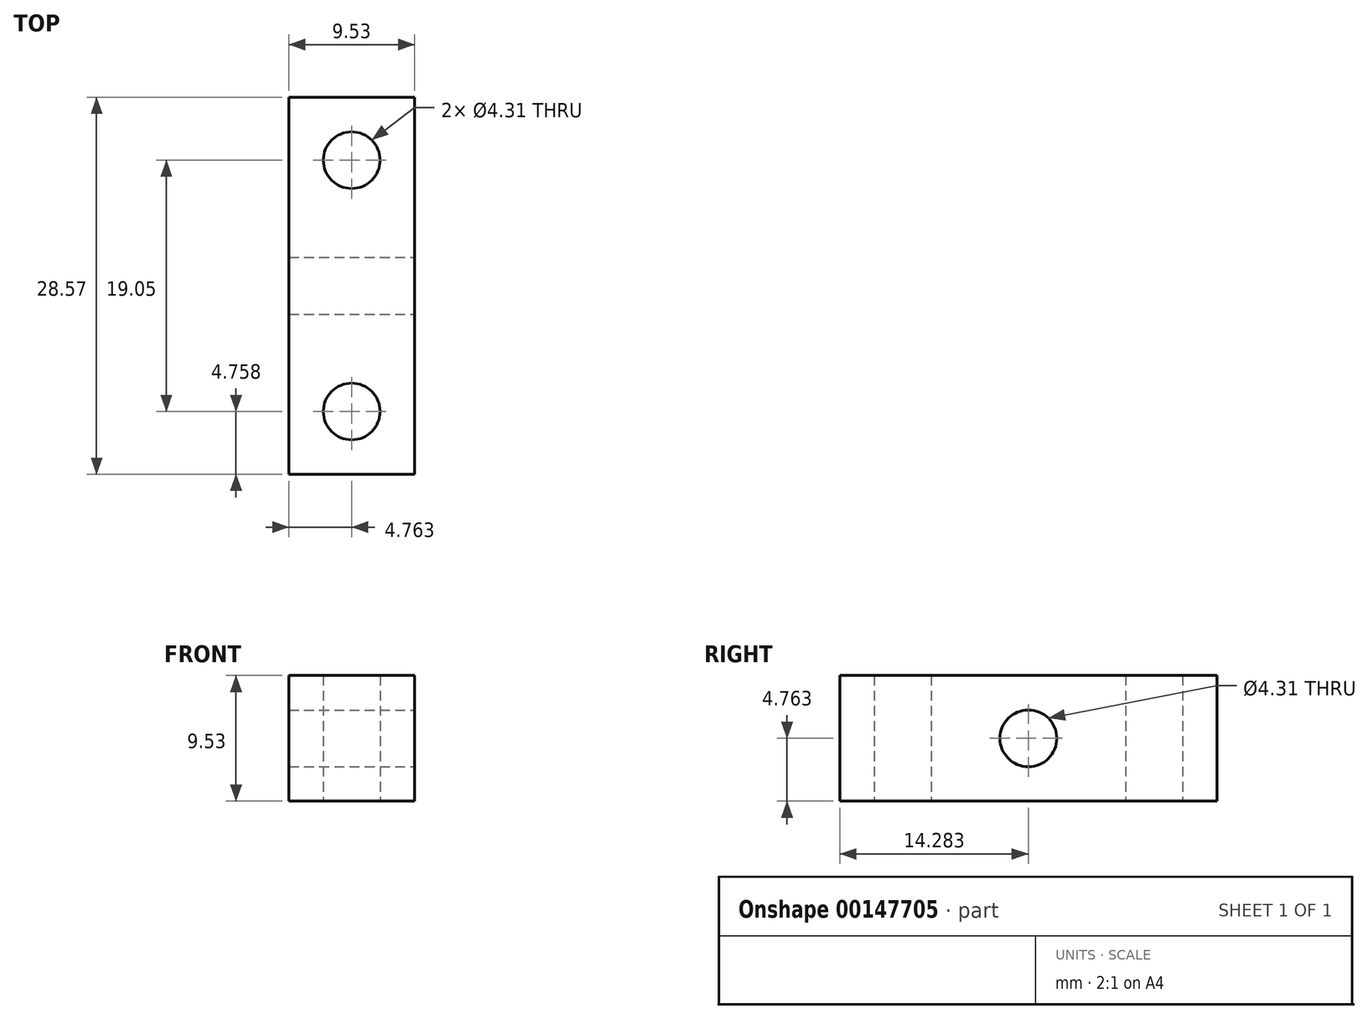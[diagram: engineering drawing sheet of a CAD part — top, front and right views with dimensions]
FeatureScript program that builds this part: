
annotation { "Feature Type Name" : "Feature", "Feature Type Description" : "" }
export const myFeature = defineFeature(function(context is Context, id is Id, definition is map)
    precondition{}
    {
        {
            var Q0;
            Q0=qCreatedBy(makeId("Top.planeOp"),FACE);
            var sketch = newSketch(context, id + "F0", { "sketchPlane" : qUnion([Q0])});
            skLineSegment(sketch, "E0.bottom", {"start": v(0, 0) * mm, "end": v(9.52, 0) * mm});
            skLineSegment(sketch, "E0.top", {"start": v(0, -28.57) * mm, "end": v(9.53, -28.57) * mm});
            skLineSegment(sketch, "E0.left", {"start": v(0, 0) * mm, "end": v(0, -28.58) * mm});
            skLineSegment(sketch, "E0.right", {"start": v(9.53, 0) * mm, "end": v(9.53, -28.57) * mm});
            skLineSegment(sketch, "E1", {"start": v(4.76, 0) * mm, "end": v(4.76, -4.76) * mm, "construction": true});
            skLineSegment(sketch, "E2", {"start": v(4.76, -4.76) * mm, "end": v(4.76, -23.81) * mm, "construction": true});
            skCircle(sketch, "E3", {"center": v(4.76, -4.76) * mm, "radius": 2.15 * mm});
            skCircle(sketch, "E4", {"center": v(4.76, -23.81) * mm, "radius": 2.15 * mm});
            skLineSegment(sketch, "E5", {"start": v(4.76, -23.81) * mm, "end": v(4.76, -28.57) * mm, "construction": true});
            skSolve(sketch);
        }
        {
            var Q0;
            Q0=qSketchRegion(id+"F0",true);
            extrude(context, id + "F1", {"entities" : qUnion([Q0]), "depth" : 9.52 * mm});
        }
        {
            var Q0;
            Q0=makeQuery(id+"F1.opExtrude","SWEPT_FACE",FACE,{"disambiguationData":[OSD([sQuery(id+"F0.wireOp",EDGE,"E0.right")])]});
            var sketch = newSketch(context, id + "F2", { "sketchPlane" : qUnion([Q0])});
            skLineSegment(sketch, "E6", {"start": v(0, 4.76) * mm, "end": v(-4.76, 4.76) * mm, "construction": true});
            skLineSegment(sketch, "E7", {"start": v(-4.76, 4.76) * mm, "end": v(-23.81, 4.76) * mm, "construction": true});
            skLineSegment(sketch, "E8", {"start": v(-4.76, 4.76) * mm, "end": v(-4.76, 9.53) * mm, "construction": true});
            skLineSegment(sketch, "E9", {"start": v(-23.81, 4.76) * mm, "end": v(-23.81, 9.53) * mm, "construction": true});
            skCircle(sketch, "E10", {"center": v(-14.29, 4.76) * mm, "radius": 2.15 * mm});
            skSolve(sketch);
        }
        {
            var Q0;
            Q0=qSketchRegion(id+"F2",true);
            var Q1;
            Q1=makeQuery(id+"F1.opExtrude","SWEPT_FACE",FACE,{"disambiguationData":[OSD([sQuery(id+"F0.wireOp",EDGE,"E0.left")])]});
            extrude(context, id + "F3", {"entities" : qUnion([Q0]), "operationType" : NewBodyOperationType.REMOVE, "endBound" : BoundingType.UP_TO_SURFACE, "oppositeDirection" : true, "endBoundEntityFace" : qUnion([Q1]), "depth" : 25.4 * mm});
        }
    });
